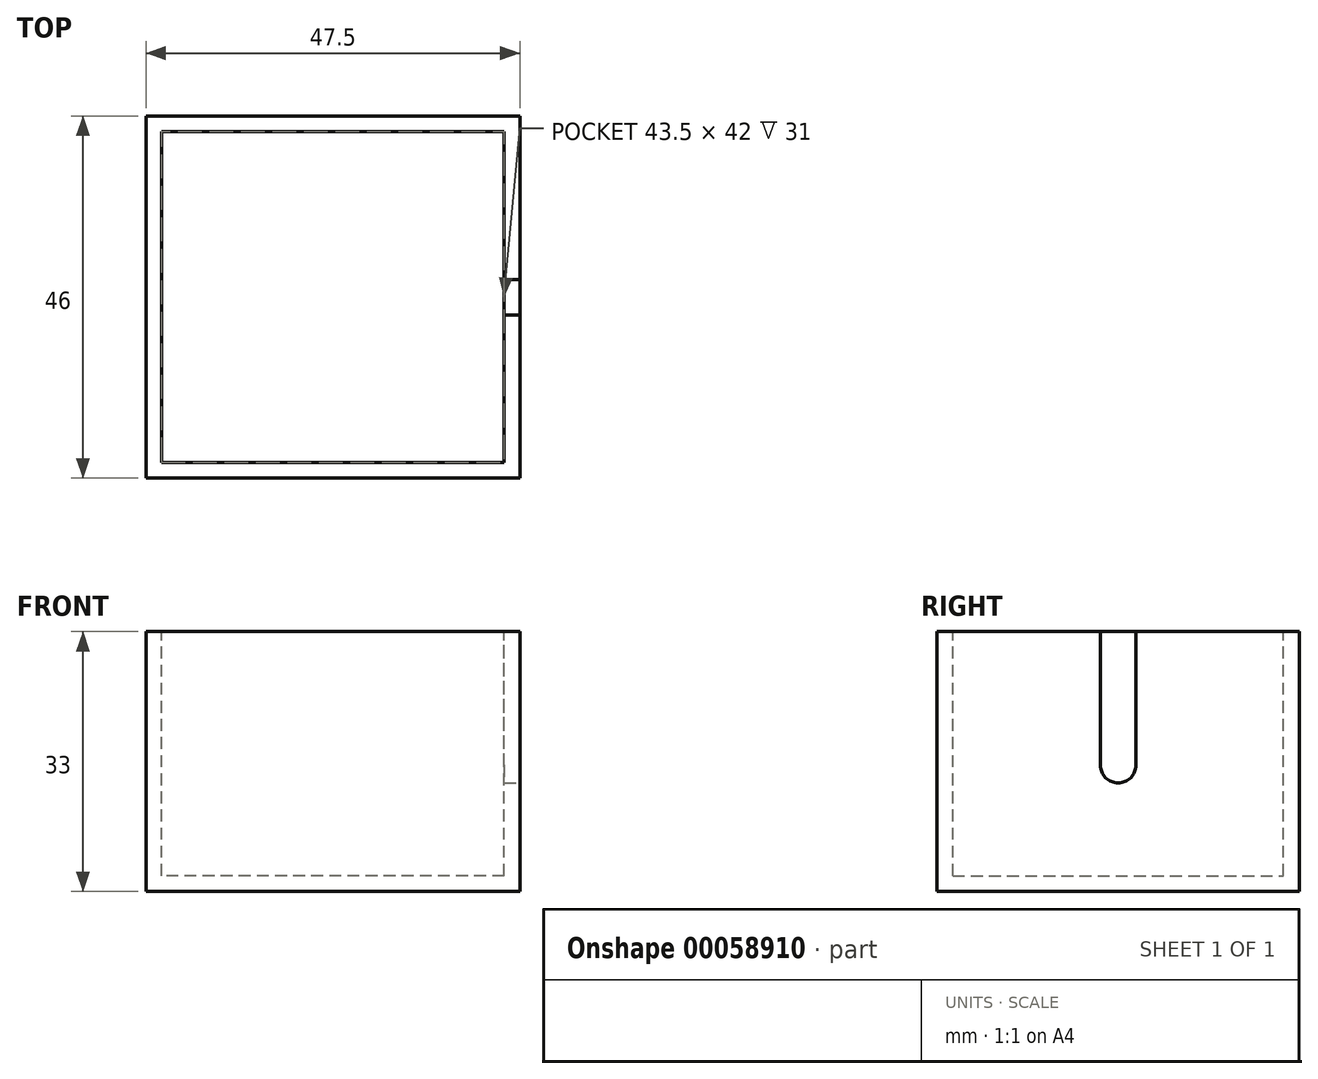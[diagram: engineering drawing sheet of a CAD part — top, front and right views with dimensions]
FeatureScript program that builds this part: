
annotation { "Feature Type Name" : "Feature", "Feature Type Description" : "" }
export const myFeature = defineFeature(function(context is Context, id is Id, definition is map)
    precondition{}
    {
        {
            var Q0;
            Q0=qCreatedBy(makeId("Top.planeOp"),FACE);
            var sketch = newSketch(context, id + "F0", { "sketchPlane" : qUnion([Q0])});
            skLineSegment(sketch, "E0.rect.bottom", {"start": v(23.75, 23) * mm, "end": v(-23.75, 23) * mm});
            skLineSegment(sketch, "E0.rect.top", {"start": v(23.75, -23) * mm, "end": v(-23.75, -23) * mm});
            skLineSegment(sketch, "E0.rect.left", {"start": v(23.75, 23) * mm, "end": v(23.75, -23) * mm});
            skLineSegment(sketch, "E0.rect.right", {"start": v(-23.75, 23) * mm, "end": v(-23.75, -23) * mm});
            skPoint(sketch, "E0.rect.middle", {"position": v(0, 0) * mm});
            skSolve(sketch);
        }
        {
            var Q0;
            Q0 = qSketchRegion(id + "F0", true);
            extrude(context, id + "F1", {"entities" : qUnion([Q0]), "depth" : 33 * mm});
        }
        {
            var Q0;
            Q0=makeQuery(id+"F1.opExtrude","CAP_FACE",FACE,{"disambiguationData":[OSD([sQuery(id+"F0.wireOp",EDGE,"E0.rect.bottom"),sQuery(id+"F0.wireOp",EDGE,"E0.rect.top"),sQuery(id+"F0.wireOp",EDGE,"E0.rect.left"),sQuery(id+"F0.wireOp",EDGE,"E0.rect.right")])],"isStart":false});
            var sketch = newSketch(context, id + "F2", { "sketchPlane" : qUnion([Q0])});
            skLineSegment(sketch, "E1.rect.bottom", {"start": v(21.75, -21) * mm, "end": v(-21.75, -21) * mm});
            skLineSegment(sketch, "E1.rect.top", {"start": v(21.75, 21) * mm, "end": v(-21.75, 21) * mm});
            skLineSegment(sketch, "E1.rect.left", {"start": v(21.75, -21) * mm, "end": v(21.75, 21) * mm});
            skLineSegment(sketch, "E1.rect.right", {"start": v(-21.75, -21) * mm, "end": v(-21.75, 21) * mm});
            skPoint(sketch, "E1.rect.middle", {"position": v(0, 0) * mm});
            skSolve(sketch);
        }
        {
            var Q0;
            Q0 = qSketchRegion(id + "F2", true);
            extrude(context, id + "F3", {"entities" : qUnion([Q0]), "operationType" : NewBodyOperationType.REMOVE, "oppositeDirection" : true, "depth" : 31 * mm});
        }
        {
            var Q0;
            Q0=makeQuery(id+"F1.opExtrude","SWEPT_FACE",FACE,{"disambiguationData":[OSD([sQuery(id+"F0.wireOp",EDGE,"E0.rect.left")])]});
            var sketch = newSketch(context, id + "F4", { "sketchPlane" : qUnion([Q0])});
            skCircle(sketch, "E2", {"center": v(0, 16.04) * mm, "radius": 2.25 * mm});
            skLineSegment(sketch, "E3", {"start": v(-2.25, 16.04) * mm, "end": v(-2.25, 33) * mm});
            skLineSegment(sketch, "E4", {"start": v(2.25, 16.04) * mm, "end": v(2.25, 33) * mm});
            skSolve(sketch);
        }
        {
            var Q0;
            {var subQ0=sQuery(id+"F4.wireOp",EDGE,"E3");Q0=makeQuery(id+"F4.imprint","IMPRINT",FACE,{"disambiguationData":[TD([[makeQuery(id+"F4.imprint","IMPRINT",EDGE,{"derivedFrom":subQ0}),-1.0]])]});}
            var Q1;
            {var subQ0=sQuery(id+"F4.wireOp",EDGE,"E2");var subQ1=makeQuery(id+"F4.imprint","INTERSECT",VERTEX,{"derivedFrom":[subQ0,sQuery(id+"F4.wireOp",EDGE,"E3")]});Q1=makeQuery(id+"F4.imprint","IMPRINT",FACE,{"disambiguationData":[TD([[makeQuery(id+"F4.imprint","IMPRINT",EDGE,{"disambiguationData":[TD([[subQ1,1.0]])],"derivedFrom":subQ0}),1.0]])]});}
            extrude(context, id + "F5", {"entities" : qUnion([Q0, Q1]), "operationType" : NewBodyOperationType.REMOVE, "oppositeDirection" : true, "depth" : 5 * mm});
        }
    });
